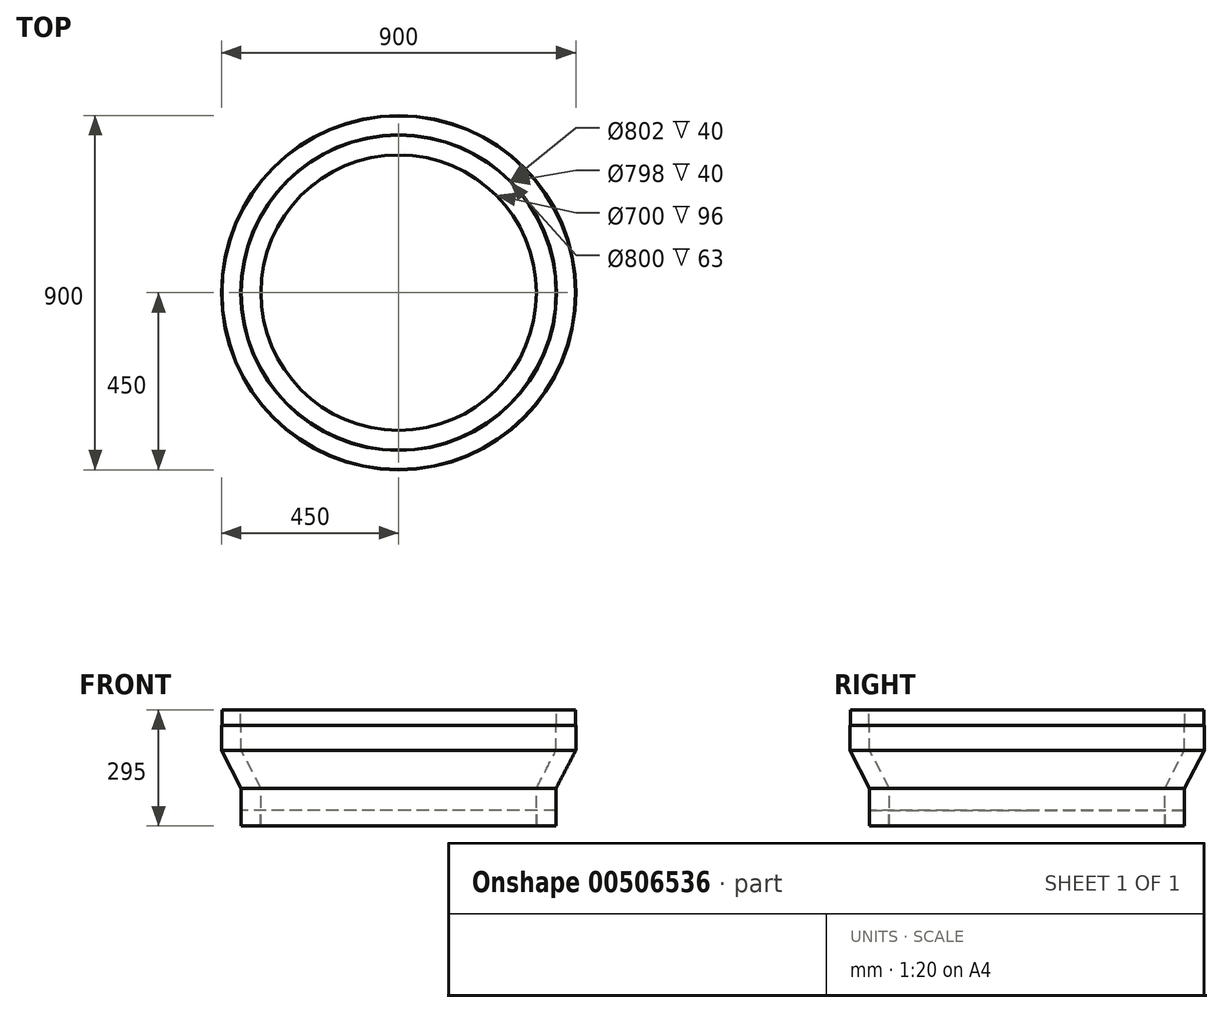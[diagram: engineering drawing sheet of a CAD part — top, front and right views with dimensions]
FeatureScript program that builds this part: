
annotation { "Feature Type Name" : "Feature", "Feature Type Description" : "" }
export const myFeature = defineFeature(function(context is Context, id is Id, definition is map)
    precondition{}
    {
        {
            var Q0;
            Q0=qCreatedBy(makeId("Front.planeOp"),FACE);
            var sketch = newSketch(context, id + "F0", { "sketchPlane" : qUnion([Q0])});
            skLineSegment(sketch, "E0", {"start": v(0, 433.08) * mm, "end": v(0, -434.74) * mm, "construction": true});
            skLineSegment(sketch, "E1", {"start": v(-350, -254.87) * mm, "end": v(-350, -158.87) * mm});
            skLineSegment(sketch, "E2", {"start": v(-350, -254.87) * mm, "end": v(-351, -254.87) * mm});
            skLineSegment(sketch, "E3", {"start": v(-351, -254.87) * mm, "end": v(-351, -214.87) * mm});
            skLineSegment(sketch, "E4", {"start": v(-351, -214.87) * mm, "end": v(-399, -214.87) * mm});
            skLineSegment(sketch, "E5", {"start": v(-399, -214.87) * mm, "end": v(-399, -254.87) * mm});
            skLineSegment(sketch, "E6", {"start": v(-399, -254.87) * mm, "end": v(-400, -254.87) * mm});
            skLineSegment(sketch, "E7", {"start": v(-400, -254.87) * mm, "end": v(-400, -158.87) * mm});
            skLineSegment(sketch, "E8", {"start": v(-449, 40.13) * mm, "end": v(-401, 40.13) * mm});
            skLineSegment(sketch, "E9", {"start": v(-401, 40.13) * mm, "end": v(-401, 0.13) * mm});
            skLineSegment(sketch, "E10", {"start": v(-401, 0.13) * mm, "end": v(-400, 0.13) * mm});
            skLineSegment(sketch, "E11", {"start": v(-400, 0.13) * mm, "end": v(-400, -62.87) * mm});
            skLineSegment(sketch, "E12", {"start": v(-449, 40.13) * mm, "end": v(-449, 0.13) * mm});
            skLineSegment(sketch, "E13", {"start": v(-449, 0.13) * mm, "end": v(-450, 0.13) * mm});
            skLineSegment(sketch, "E14", {"start": v(-450, 0.13) * mm, "end": v(-450, -62.87) * mm});
            skLineSegment(sketch, "E15", {"start": v(-400, -62.87) * mm, "end": v(-350, -158.87) * mm});
            skLineSegment(sketch, "E16", {"start": v(-450, -62.87) * mm, "end": v(-400, -158.87) * mm});
            skSolve(sketch);
        }
        {
            var Q0;
            Q0=qSketchRegion(id+"F0",true);
            var Q1;
            Q1=sQuery(id+"F0.wireOp",EDGE,"E0");
            revolve(context, id + "F1", {"entities" : qUnion([Q0]), "axis" : qUnion([Q1]), "revolveType" : RevolveType.FULL});
        }
    });
